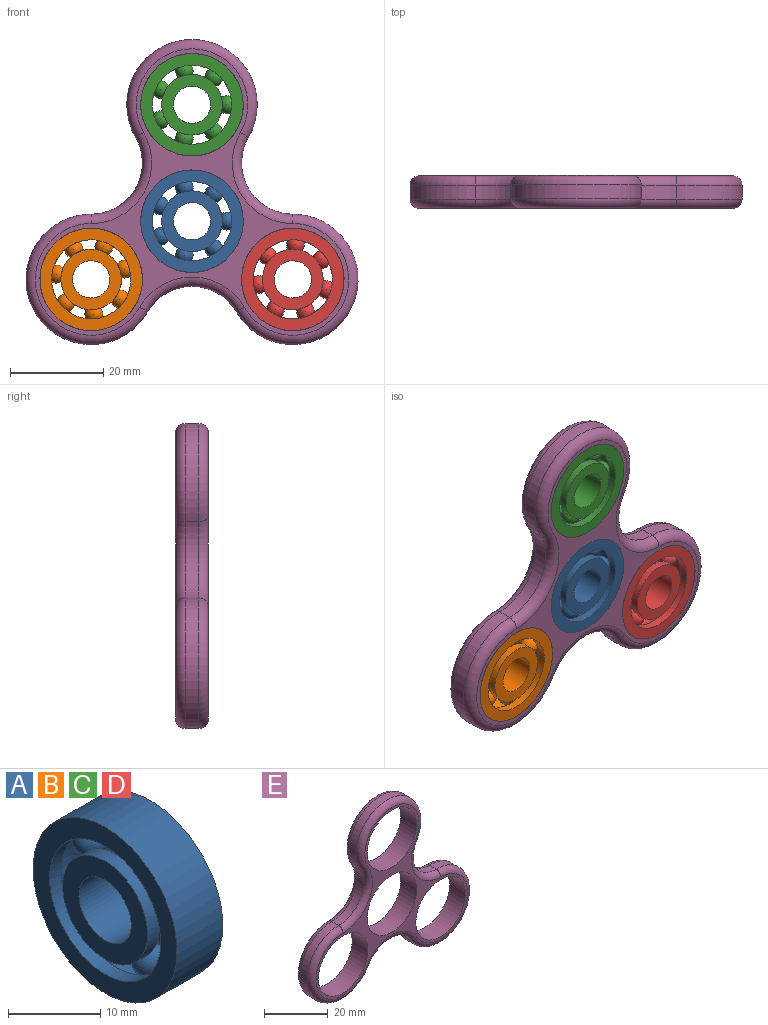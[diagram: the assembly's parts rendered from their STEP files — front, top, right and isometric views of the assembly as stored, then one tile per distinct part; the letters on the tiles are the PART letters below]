
ASSEMBLY  parts=5 mates=2
PART A: 55 faces, bbox 7x22x22 mm
  f0: cylinder r=6.5mm len=13mm, axis (-1,0,0), area 72.2mm2, adj f1,f2,f3,f4,f5,f6,f7,f8
  f1: plane 13x13mm, normal (1,0,0), area 82.5mm2, adj f0,f16
  f2: torus R=0.08mm, axis (-1,0,0), area 2.3mm2, adj f0,f3,f15,f17
  f3: torus R=7.5mm, axis (-1,0,0), area 18.1mm2, adj f0,f2,f4,f17,f18,f19
  f4: torus R=0.08mm, axis (-1,0,0), area 2.3mm2, adj f0,f3,f5,f18
  f5: torus R=7.5mm, axis (-1,0,0), area 18.1mm2, adj f0,f4,f6,f18,f19,f20
  f6: torus R=0.08mm, axis (-1,0,0), area 2.3mm2, adj f0,f5,f7,f20
  f7: torus R=7.5mm, axis (-1,0,0), area 18.1mm2, adj f0,f6,f8,f19,f20,f21
  f8: torus R=0.08mm, axis (-1,0,0), area 2.3mm2, adj f0,f7,f9,f21
  f9: torus R=7.5mm, axis (-1,0,0), area 18.1mm2, adj f0,f8,f10,f19,f21,f22
  f10: torus R=0.08mm, axis (-1,0,0), area 2.3mm2, adj f0,f9,f11,f22
  f11: torus R=7.5mm, axis (-1,0,0), area 18.1mm2, adj f0,f10,f12,f19,f22,f23
  f12: torus R=0.08mm, axis (-1,0,0), area 2.3mm2, adj f0,f11,f13,f23
  f13: torus R=7.5mm, axis (-1,0,0), area 18.1mm2, adj f0,f12,f14,f19,f23,f24
  f14: torus R=0.08mm, axis (-1,0,0), area 2.3mm2, adj f0,f13,f15,f24
  f15: torus R=7.5mm, axis (-1,0,0), area 18.1mm2, adj f0,f2,f14,f17,f19,f24
  f16: cylinder r=4mm len=8mm, axis (-1,0,0), area 175.9mm2, adj f1,f25
  f17: torus R=0.08mm, axis (-1,0,0), area 2.3mm2, adj f2,f3,f15,f19
  f18: torus R=0.08mm, axis (-1,0,0), area 2.3mm2, adj f3,f4,f5,f19
  f19: cylinder r=6.5mm len=13mm, axis (-1,0,0), area 72.2mm2, adj f3,f5,f7,f9,f11,f13,f15,f17
  f20: torus R=0.08mm, axis (-1,0,0), area 2.3mm2, adj f5,f6,f7,f19
  f21: torus R=0.08mm, axis (-1,0,0), area 2.3mm2, adj f7,f8,f9,f19
  f22: torus R=0.08mm, axis (-1,0,0), area 2.3mm2, adj f9,f10,f11,f19
  f23: torus R=0.08mm, axis (-1,0,0), area 2.3mm2, adj f11,f12,f13,f19
  f24: torus R=0.08mm, axis (-1,0,0), area 2.3mm2, adj f13,f14,f15,f19
  f25: plane 13x13mm, normal (-1,0,0), area 82.5mm2, adj f16,f19
  f26: cylinder r=8.5mm len=17mm, axis (-1,0,0), area 94.3mm2, adj f27,f28,f29,f30,f31,f32,f33,f34
  f27: plane 22x22mm, normal (1,0,0), area 153.2mm2, adj f26,f45
  f28: torus R=0.08mm, axis (-1,0,0), area 2.3mm2, adj f26,f29,f44,f46
  f29: torus R=7.5mm, axis (-1,0,0), area 30.4mm2, adj f26,f28,f30,f46
  f30: torus R=0.08mm, axis (-1,0,0), area 4.6mm2, adj f26,f29,f31,f46
  f31: torus R=7.5mm, axis (-1,0,0), area 30.4mm2, adj f26,f30,f32,f46
  f32: torus R=0.08mm, axis (-1,0,0), area 4.6mm2, adj f26,f31,f33,f46
  f33: torus R=7.5mm, axis (-1,0,0), area 30.4mm2, adj f26,f32,f35,f46
  f34: torus R=0.08mm, axis (-1,0,0), area 2.3mm2, adj f26,f35,f36,f46
  f35: torus R=0.08mm, axis (-1,0,0), area 2.3mm2, adj f26,f33,f34,f46
  f36: torus R=7.5mm, axis (-1,0,0), area 30.4mm2, adj f26,f34,f37,f46
  f37: torus R=0.08mm, axis (-1,0,0), area 4.6mm2, adj f26,f36,f38,f46
  f38: torus R=7.5mm, axis (-1,0,0), area 30.4mm2, adj f26,f37,f40,f46
  f39: torus R=0.08mm, axis (-1,0,0), area 2.3mm2, adj f26,f40,f41,f46
  f40: torus R=0.08mm, axis (-1,0,0), area 2.3mm2, adj f26,f38,f39,f46
  f41: torus R=7.5mm, axis (-1,0,0), area 30.4mm2, adj f26,f39,f42,f46
  f42: torus R=0.08mm, axis (-1,0,0), area 4.6mm2, adj f26,f41,f43,f46
  f43: torus R=7.5mm, axis (-1,0,0), area 30.4mm2, adj f26,f42,f44,f46
  f44: torus R=0.08mm, axis (-1,0,0), area 2.3mm2, adj f26,f28,f43,f46
  f45: cylinder r=11mm len=22mm, axis (-1,0,0), area 483.8mm2, adj f27,f47
  f46: cylinder r=8.5mm len=17mm, axis (-1,0,0), area 94.3mm2, adj f28,f29,f30,f31,f32,f33,f34,f35
  f47: plane 22x22mm, normal (-1,0,0), area 153.2mm2, adj f45,f46
  f48: torus R=0.08mm, axis (-1,0,0), area 47.3mm2
  f49: torus R=0.08mm, axis (-1,0,0), area 47.3mm2
  f50: torus R=0.08mm, axis (-1,0,0), area 47.3mm2
  f51: torus R=0.08mm, axis (-1,0,0), area 47.3mm2
  f52: torus R=0.08mm, axis (-1,0,0), area 47.3mm2
  f53: torus R=0.08mm, axis (-1,0,0), area 47.3mm2
  f54: torus R=0.08mm, axis (-1,0,0), area 47.3mm2
PART B: same geometry as A
PART C: same geometry as A
PART D: same geometry as A
PART E: 24 faces, bbox 73.6x7x67.8 mm
  f0: cylinder r=11mm len=16.5mm, axis (0,1,0), area 69.1mm2, adj f1,f9,f13,f22
  f1: cylinder r=14mm len=28mm, axis (0,1,0), area 175.9mm2, adj f0,f2,f12,f20
  f2: cylinder r=11mm len=16.5mm, axis (0,1,0), area 69.1mm2, adj f1,f3,f14,f18
  f3: cylinder r=14mm len=28mm, axis (0,1,0), area 175.9mm2, adj f2,f4,f16,f19
  f4: cylinder r=11mm len=19.05mm, axis (0,1,0), area 69.1mm2, adj f3,f9,f17,f21
  f5: cylinder r=11mm len=22mm, axis (0,1,0), area 483.8mm2, adj f10,f11
  f6: cylinder r=11mm len=22mm, axis (0,1,0), area 483.8mm2, adj f10,f11
  f7: cylinder r=11mm len=22mm, axis (0,1,0), area 483.8mm2, adj f10,f11
  f8: cylinder r=11mm len=22mm, axis (0,1,0), area 483.8mm2, adj f10,f11
  f9: cylinder r=14mm len=28mm, axis (0,1,0), area 175.9mm2, adj f0,f4,f15,f23
  f10: plane 67.3x61.5mm, normal (0,-1,0), area 477.1mm2, adj f5,f6,f7,f8,f18,f19,f20,f21
  f11: plane 67.3x61.5mm, normal (0,1,0), area 477.1mm2, adj f5,f6,f7,f8,f12,f13,f14,f15
  f12: torus R=12mm, axis (0,-1,0), area 174.7mm2, adj f1,f11,f13,f14
  f13: torus R=13mm, axis (0,-1,0), area 77.2mm2, adj f0,f11,f12,f15
  f14: torus R=13mm, axis (0,-1,0), area 77.2mm2, adj f2,f11,f12,f16
  f15: torus R=12mm, axis (0,-1,0), area 174.7mm2, adj f9,f11,f13,f17
  f16: torus R=12mm, axis (0,-1,0), area 174.7mm2, adj f3,f11,f14,f17
  f17: torus R=13mm, axis (0,-1,0), area 77.2mm2, adj f4,f11,f15,f16
  f18: torus R=13mm, axis (0,-1,0), area 77.2mm2, adj f2,f10,f19,f20
  f19: torus R=12mm, axis (0,-1,0), area 174.7mm2, adj f3,f10,f18,f21
  f20: torus R=12mm, axis (0,-1,0), area 174.7mm2, adj f1,f10,f18,f22
  f21: torus R=13mm, axis (0,-1,0), area 77.2mm2, adj f4,f10,f19,f23
  f22: torus R=13mm, axis (0,-1,0), area 77.2mm2, adj f0,f10,f20,f23
  f23: torus R=12mm, axis (0,-1,0), area 174.7mm2, adj f9,f10,f21,f22
PLACE A rot(axis=(-0.58,0.58,-0.58),120deg) t=(3.89,0.07,-0.88)mm
PLACE B rot(axis=(0.25,-0.25,-0.94),93.8deg) t=(-17.76,0.07,-13.38)mm
PLACE C rot(axis=(-0.58,0.58,-0.58),120deg) t=(3.89,0.07,24.12)mm
PLACE D rot(axis=(0.69,-0.69,-0.19),158.9deg) t=(25.54,0.07,-13.38)mm
PLACE E t=(3.89,0.07,-0.88)mm fixed
MATE fastened A.f0 <-> E.f6  axis (0,-1,0) through (3.89,-3.43,-0.88)mm
MATE fastened C.f0 <-> E.f5  axis (0,-1,0) through (3.89,-3.43,24.12)mm
